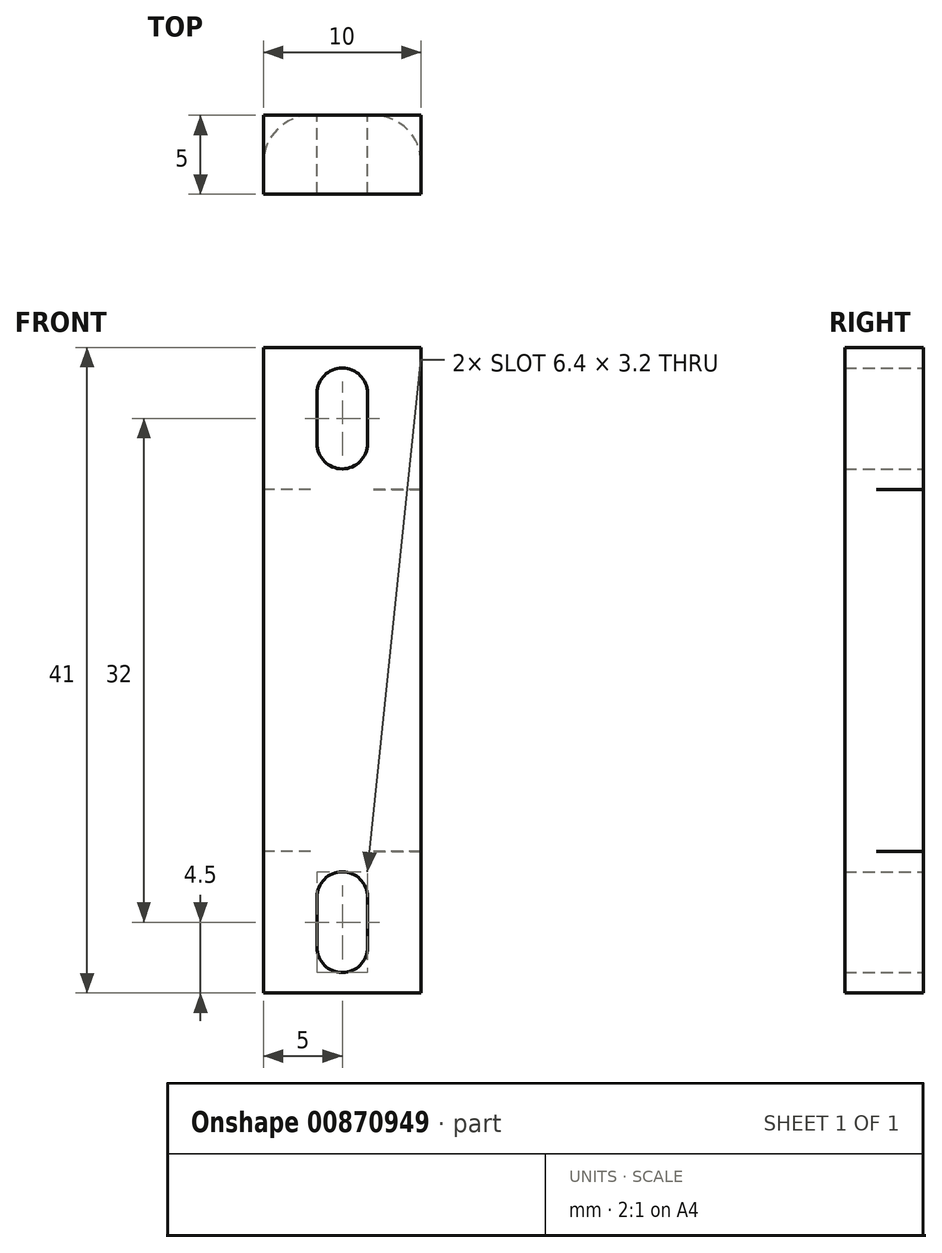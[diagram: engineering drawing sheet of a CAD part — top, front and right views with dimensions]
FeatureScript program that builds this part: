
annotation { "Feature Type Name" : "Feature", "Feature Type Description" : "" }
export const myFeature = defineFeature(function(context is Context, id is Id, definition is map)
    precondition{}
    {
        {
            var Q0;
            Q0=qCreatedBy(makeId("Front.planeOp"),FACE);
            var sketch = newSketch(context, id + "F0", { "sketchPlane" : qUnion([Q0])});
            skLineSegment(sketch, "E0.bottom", {"start": v(0, 0) * mm, "end": v(10, 0) * mm});
            skLineSegment(sketch, "E0.top", {"start": v(0, 41) * mm, "end": v(10, 41) * mm});
            skLineSegment(sketch, "E0.left", {"start": v(0, 0) * mm, "end": v(0, 41) * mm});
            skLineSegment(sketch, "E0.right", {"start": v(10, 0) * mm, "end": v(10, 41) * mm});
            skLineSegment(sketch, "E1", {"start": v(10, 20.5) * mm, "end": v(0, 20.5) * mm, "construction": true});
            skLineSegment(sketch, "E2", {"start": v(5, 20.5) * mm, "end": v(5, 36.5) * mm, "construction": true});
            skLineSegment(sketch, "E3", {"start": v(5, 20.5) * mm, "end": v(5, 4.5) * mm, "construction": true});
            skArc(sketch, "E4", {"start": v(3.4, 34.9) * mm, "mid": v(5, 33.3) * mm, "end": v(6.6, 34.9) * mm});
            skArc(sketch, "E5", {"start": v(6.6, 38.1) * mm, "mid": v(5, 39.7) * mm, "end": v(3.4, 38.1) * mm});
            skLineSegment(sketch, "E6", {"start": v(3.4, 38.1) * mm, "end": v(3.4, 34.9) * mm});
            skLineSegment(sketch, "E7", {"start": v(6.6, 38.1) * mm, "end": v(6.6, 34.9) * mm});
            skArc(sketch, "E8", {"start": v(6.6, 6.1) * mm, "mid": v(5, 7.7) * mm, "end": v(3.4, 6.1) * mm});
            skArc(sketch, "E9", {"start": v(3.4, 2.9) * mm, "mid": v(5, 1.3) * mm, "end": v(6.6, 2.9) * mm});
            skPoint(sketch, "E9.centerSnap0", {"position": v(5, 0) * mm});
            skLineSegment(sketch, "E10", {"start": v(3.4, 6.1) * mm, "end": v(3.4, 2.9) * mm});
            skLineSegment(sketch, "E11", {"start": v(6.6, 6.1) * mm, "end": v(6.6, 2.9) * mm});
            skSolve(sketch);
        }
        {
            var Q0;
            Q0=makeQuery(id+"F0.imprint","IMPRINT",FACE,{"disambiguationData":[TD([[makeQuery(id+"F0.imprint","IMPRINT",EDGE,{"derivedFrom":sQuery(id+"F0.wireOp",EDGE,"E0.bottom")}),1.0]])]});
            extrude(context, id + "F1", {"entities" : qUnion([Q0]), "depth" : 5 * mm, "offsetDistance" : 25 * mm});
        }
        {
            var Q0;
            Q0=qCreatedBy(makeId("Top.planeOp"),FACE);
            cPlane(context, id + "F2", {"entities" : qUnion([Q0]), "cplaneType" : CPlaneType.OFFSET, "offset" : 9 * mm, "width" : 150 * mm, "height" : 150 * mm});
        }
        {
            var Q0;
            Q0=qCreatedBy(id+"F2.planeOp",FACE);
            var sketch = newSketch(context, id + "F3", { "sketchPlane" : qUnion([Q0])});
            skLineSegment(sketch, "E12.0", {"start": v(3, 0) * mm, "end": v(7, 0) * mm});
            skPoint(sketch, "E13.0", {"position": v(10, -2.5) * mm});
            skLineSegment(sketch, "E14.0", {"start": v(10, -5) * mm, "end": v(10, -3) * mm});
            skLineSegment(sketch, "E15.0", {"start": v(0, -5) * mm, "end": v(0, -3) * mm});
            skPoint(sketch, "E16.visualSharp", {"position": v(0, 0) * mm});
            skArc(sketch, "E16.filletArc", {"start": v(3, 0) * mm, "mid": v(0.88, -0.88) * mm, "end": v(0, -3) * mm});
            skPoint(sketch, "E17.visualSharp", {"position": v(10, 0) * mm});
            skArc(sketch, "E17.filletArc", {"start": v(10, -3) * mm, "mid": v(9.12, -0.88) * mm, "end": v(7, 0) * mm});
            skLineSegment(sketch, "E18", {"start": v(0, -3) * mm, "end": v(0, 0) * mm});
            skLineSegment(sketch, "E19", {"start": v(3, 0) * mm, "end": v(0, 0) * mm});
            skLineSegment(sketch, "E20", {"start": v(7, 0) * mm, "end": v(10, 0) * mm});
            skLineSegment(sketch, "E21", {"start": v(10, 0) * mm, "end": v(10, -2.5) * mm});
            skLineSegment(sketch, "E22", {"start": v(10, -2.5) * mm, "end": v(10, -3) * mm});
            skSolve(sketch);
        }
        {
            var Q0;
            Q0 = qSketchRegion(id + "F3", true);
            extrude(context, id + "F4", {"entities" : qUnion([Q0]), "operationType" : NewBodyOperationType.REMOVE, "depth" : 23 * mm, "offsetDistance" : 25 * mm});
        }
    });
